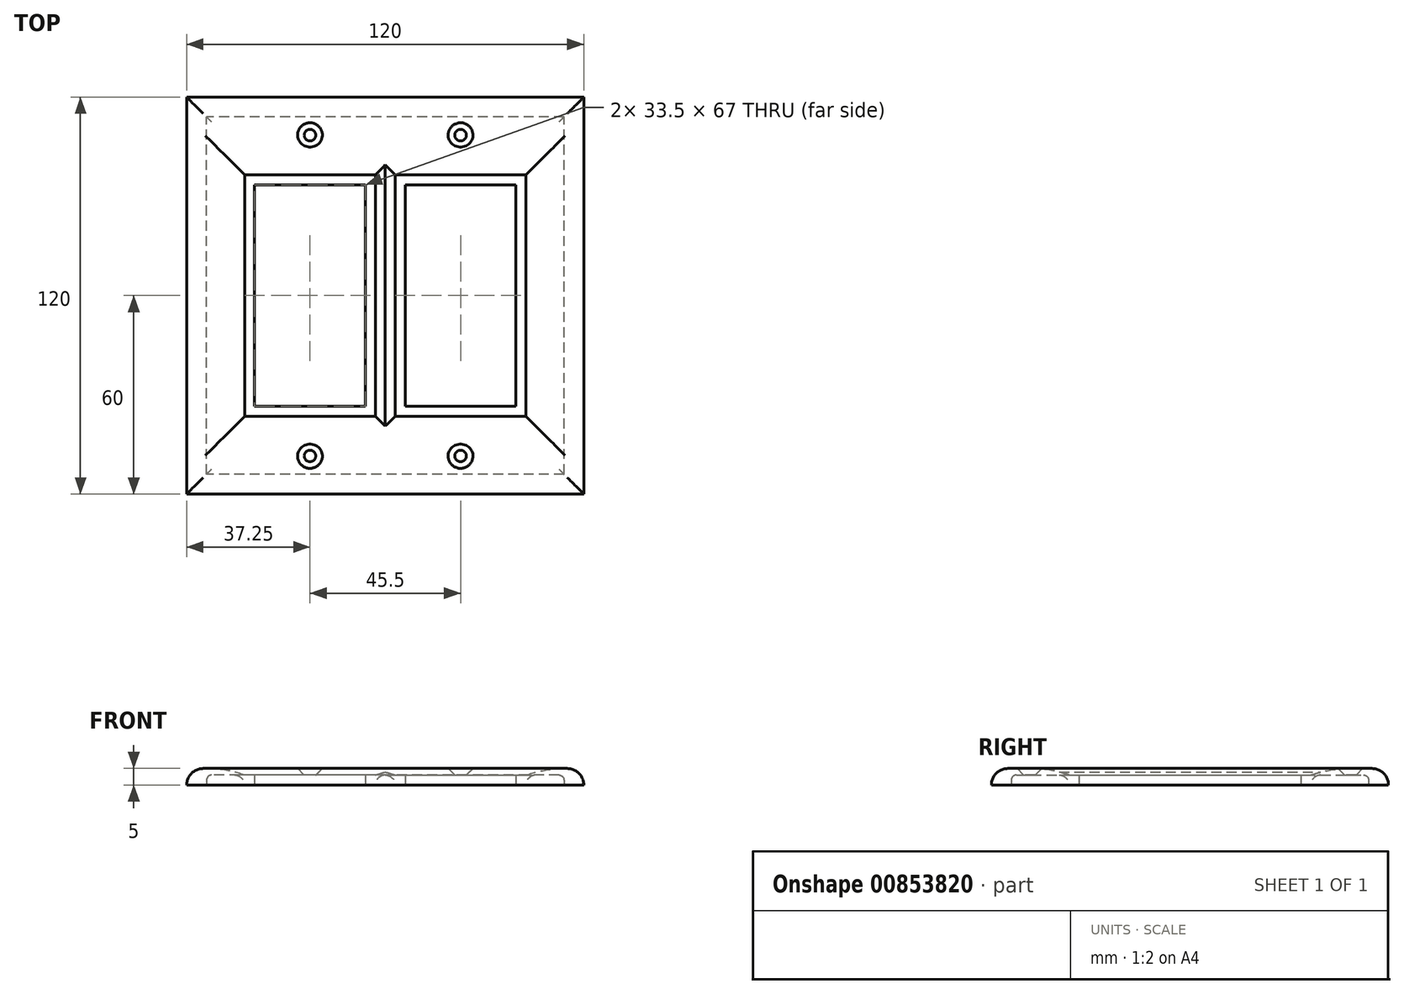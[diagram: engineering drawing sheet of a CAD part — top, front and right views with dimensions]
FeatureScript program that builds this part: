
annotation { "Feature Type Name" : "Feature", "Feature Type Description" : "" }
export const myFeature = defineFeature(function(context is Context, id is Id, definition is map)
    precondition{}
    {
        {
            var Q0;
            Q0=qCreatedBy(makeId("Top.planeOp"),FACE);
            var sketch = newSketch(context, id + "F0", { "sketchPlane" : qUnion([Q0])});
            skLineSegment(sketch, "E0.bottom", {"start": v(60, -60) * mm, "end": v(-60, -60) * mm});
            skLineSegment(sketch, "E0.top", {"start": v(60, 60) * mm, "end": v(-60, 60) * mm});
            skLineSegment(sketch, "E0.left", {"start": v(60, -60) * mm, "end": v(60, 60) * mm});
            skLineSegment(sketch, "E0.right", {"start": v(-60, -60) * mm, "end": v(-60, 60) * mm});
            skPoint(sketch, "E0.middle", {"position": v(0, 0) * mm});
            skLineSegment(sketch, "E1", {"start": v(0, 60) * mm, "end": v(0, -60) * mm, "construction": true});
            skLineSegment(sketch, "E2.bottom", {"start": v(-6, -33.5) * mm, "end": v(-39.5, -33.5) * mm});
            skLineSegment(sketch, "E2.top", {"start": v(-6, 33.5) * mm, "end": v(-39.5, 33.5) * mm});
            skLineSegment(sketch, "E2.left", {"start": v(-6, -33.5) * mm, "end": v(-6, 33.5) * mm});
            skLineSegment(sketch, "E2.right", {"start": v(-39.5, -33.5) * mm, "end": v(-39.5, 33.5) * mm});
            skPoint(sketch, "E2.middle", {"position": v(-22.75, 0) * mm});
            skLineSegment(sketch, "E3", {"start": v(-22.75, 60) * mm, "end": v(-22.75, -60) * mm, "construction": true});
            skPoint(sketch, "E3.startSnap0", {"position": v(-22.75, 33.5) * mm});
            skPoint(sketch, "E3.endSnap0", {"position": v(-22.75, -33.5) * mm});
            skCircle(sketch, "E4", {"center": v(-22.75, 48.5) * mm, "radius": 1.75 * mm});
            skLineSegment(sketch, "E5", {"start": v(-56.43, 0) * mm, "end": v(49.83, 0) * mm, "construction": true});
            skPoint(sketch, "E5.endSnap0", {"position": v(-6, 0) * mm});
            skCircle(sketch, "E6.MirrorC", {"center": v(-22.75, -48.5) * mm, "radius": 1.75 * mm});
            skLineSegment(sketch, "E7.MirrorCS", {"start": v(-6, 60) * mm, "end": v(-6, 33.5) * mm});
            skLineSegment(sketch, "E8.MirrorCS", {"start": v(6, 33.5) * mm, "end": v(39.5, 33.5) * mm});
            skLineSegment(sketch, "E9.MirrorCS", {"start": v(6, -33.5) * mm, "end": v(6, 33.5) * mm});
            skLineSegment(sketch, "E10.MirrorCS", {"start": v(39.5, -33.5) * mm, "end": v(39.5, 33.5) * mm});
            skLineSegment(sketch, "E11.MirrorCS", {"start": v(6, -33.5) * mm, "end": v(39.5, -33.5) * mm});
            skCircle(sketch, "E12.MirrorC", {"center": v(22.75, -48.5) * mm, "radius": 1.75 * mm});
            skCircle(sketch, "E13.MirrorC", {"center": v(22.75, 48.5) * mm, "radius": 1.75 * mm});
            skLineSegment(sketch, "E14.0", {"start": v(54, 54) * mm, "end": v(-54, 54) * mm});
            skLineSegment(sketch, "E14.1", {"start": v(54, -54) * mm, "end": v(54, 54) * mm});
            skLineSegment(sketch, "E14.2", {"start": v(54, -54) * mm, "end": v(-54, -54) * mm});
            skLineSegment(sketch, "E14.3", {"start": v(-54, -54) * mm, "end": v(-54, 54) * mm});
            skPoint(sketch, "E15.MirrorCS.end.orphan", {"position": v(-39.5, 100.5) * mm});
            skPoint(sketch, "E15.MirrorCS.start.orphan", {"position": v(-6, 100.5) * mm});
            skLineSegment(sketch, "E16.0", {"start": v(-42.5, -36.5) * mm, "end": v(-42.5, 36.5) * mm});
            skLineSegment(sketch, "E16.1", {"start": v(-3, -36.5) * mm, "end": v(-42.5, -36.5) * mm});
            skLineSegment(sketch, "E16.2", {"start": v(-3, -36.5) * mm, "end": v(-3, 36.5) * mm});
            skLineSegment(sketch, "E16.3", {"start": v(-3, 36.5) * mm, "end": v(-42.5, 36.5) * mm});
            skLineSegment(sketch, "E17.MirrorCS", {"start": v(3, 36.5) * mm, "end": v(42.5, 36.5) * mm});
            skLineSegment(sketch, "E18.MirrorCS", {"start": v(3, -36.5) * mm, "end": v(3, 36.5) * mm});
            skLineSegment(sketch, "E19.MirrorCS", {"start": v(3, -36.5) * mm, "end": v(42.5, -36.5) * mm});
            skLineSegment(sketch, "E20.MirrorCS", {"start": v(42.5, -36.5) * mm, "end": v(42.5, 36.5) * mm});
            skSolve(sketch);
        }
        {
            var Q0;
            Q0=makeQuery(id+"F0.imprint","IMPRINT",FACE,{"disambiguationData":[TD([[makeQuery(id+"F0.imprint","IMPRINT",EDGE,{"derivedFrom":sQuery(id+"F0.wireOp",EDGE,"E2.bottom")}),1.0]])]});
            var Q1;
            Q1=makeQuery(id+"F0.imprint","IMPRINT",FACE,{"disambiguationData":[TD([[makeQuery(id+"F0.imprint","IMPRINT",EDGE,{"derivedFrom":sQuery(id+"F0.wireOp",EDGE,"E0.bottom")}),-1.0]])]});
            var Q2;
            Q2=makeQuery(id+"F0.imprint","IMPRINT",FACE,{"disambiguationData":[TD([[makeQuery(id+"F0.imprint","IMPRINT",EDGE,{"derivedFrom":sQuery(id+"F0.wireOp",EDGE,"z3IelOHg-C2kR-4Iwb-KN7V-9xO7rj5dRlTz")}),1.0]])]});
            var Q3;
            Q3=makeQuery(id+"F0.imprint","IMPRINT",FACE,{"disambiguationData":[TD([[makeQuery(id+"F0.imprint","IMPRINT",EDGE,{"derivedFrom":sQuery(id+"F0.wireOp",EDGE,"9c88f91e-e929-4360-bad2-47fe56c0c12e0.MirrorC")}),-1.0]])]});
            var Q4;
            Q4=makeQuery(id+"F0.imprint","IMPRINT",FACE,{"disambiguationData":[TD([[makeQuery(id+"F0.imprint","IMPRINT",EDGE,{"derivedFrom":sQuery(id+"F0.wireOp",EDGE,"E8.MirrorCS")}),1.0]])]});
            var Q5;
            Q5=makeQuery(id+"F0.imprint","IMPRINT",FACE,{"disambiguationData":[TD([[makeQuery(id+"F0.imprint","IMPRINT",EDGE,{"derivedFrom":sQuery(id+"F0.wireOp",EDGE,"E4")}),-1.0]])]});
            extrude(context, id + "F1", {"entities" : qUnion([Q0, Q1, Q2, Q3, Q4, Q5]), "depth" : 5 * mm, "offsetDistance" : 25 * mm});
        }
        {
            var Q0;
            Q0=makeQuery(id+"F0.imprint","IMPRINT",FACE,{"disambiguationData":[TD([[makeQuery(id+"F0.imprint","IMPRINT",EDGE,{"derivedFrom":sQuery(id+"F0.wireOp",EDGE,"E4")}),-1.0]])]});
            extrude(context, id + "F2", {"entities" : qUnion([Q0]), "operationType" : NewBodyOperationType.REMOVE, "depth" : 3 * mm, "offsetDistance" : 25 * mm});
        }
        {
            var Q0;
            Q0=makeQuery(id+"F1.opExtrude","CAP_EDGE",EDGE,{"disambiguationData":[OSD([sQuery(id+"F0.wireOp",EDGE,"E0.bottom")])],"isStart":false});
            var Q1;
            Q1=makeQuery(id+"F1.opExtrude","CAP_EDGE",EDGE,{"disambiguationData":[OSD([sQuery(id+"F0.wireOp",EDGE,"E0.left")])],"isStart":false});
            var Q2;
            Q2=makeQuery(id+"F1.opExtrude","CAP_EDGE",EDGE,{"disambiguationData":[OSD([sQuery(id+"F0.wireOp",EDGE,"E0.right")])],"isStart":false});
            var Q3;
            Q3=makeQuery(id+"F1.opExtrude","CAP_EDGE",EDGE,{"disambiguationData":[OSD([sQuery(id+"F0.wireOp",EDGE,"E0.top")])],"isStart":false});
            fillet(context, id + "F3", {"entities" : qUnion([Q0, Q1, Q2, Q3]), "radius" : 5 * mm, "tangentPropagation" : true, "allowEdgeOverflow" : false});
        }
        {
            var Q0;
            Q0=makeQuery(id+"F2.boolean.opBoolean","COPY",EDGE,{"derivedFrom":makeQuery(id+"F2.opExtrude","CAP_EDGE",EDGE,{"disambiguationData":[OSD([sQuery(id+"F0.wireOp",EDGE,"E14.0")])],"isStart":false})});
            var Q1;
            Q1=makeQuery(id+"F2.boolean.opBoolean","COPY",EDGE,{"derivedFrom":makeQuery(id+"F2.opExtrude","CAP_EDGE",EDGE,{"disambiguationData":[OSD([sQuery(id+"F0.wireOp",EDGE,"E14.1")])],"isStart":false})});
            var Q2;
            Q2=makeQuery(id+"F2.boolean.opBoolean","COPY",EDGE,{"derivedFrom":makeQuery(id+"F2.opExtrude","CAP_EDGE",EDGE,{"disambiguationData":[OSD([sQuery(id+"F0.wireOp",EDGE,"E14.2")])],"isStart":false})});
            var Q3;
            Q3=makeQuery(id+"F2.boolean.opBoolean","COPY",EDGE,{"derivedFrom":makeQuery(id+"F2.opExtrude","CAP_EDGE",EDGE,{"disambiguationData":[OSD([sQuery(id+"F0.wireOp",EDGE,"E14.3")])],"isStart":false})});
            fillet(context, id + "F4", {"entities" : qUnion([Q0, Q1, Q2, Q3]), "radius" : 1.5 * mm, "tangentPropagation" : true, "allowEdgeOverflow" : false});
        }
        {
            var Q0;
            Q0=makeQuery(id+"F1.opExtrude","CAP_EDGE",EDGE,{"disambiguationData":[OSD([sQuery(id+"F0.wireOp",EDGE,"E6.MirrorC")])],"isStart":false});
            var Q1;
            Q1=makeQuery(id+"F1.opExtrude","CAP_EDGE",EDGE,{"disambiguationData":[OSD([sQuery(id+"F0.wireOp",EDGE,"E12.MirrorC")])],"isStart":false});
            var Q2;
            Q2=makeQuery(id+"F1.opExtrude","CAP_EDGE",EDGE,{"disambiguationData":[OSD([sQuery(id+"F0.wireOp",EDGE,"E4")])],"isStart":false});
            var Q3;
            Q3=makeQuery(id+"F1.opExtrude","CAP_EDGE",EDGE,{"disambiguationData":[OSD([sQuery(id+"F0.wireOp",EDGE,"E13.MirrorC")])],"isStart":false});
            chamfer(context, id + "F5", {"entities" : qUnion([Q0, Q1, Q2, Q3]), "width" : 2 * mm, "tangentPropagation" : true});
        }
        {
            var Q0;
            Q0=makeQuery(id+"F2.boolean.opBoolean","COPY",EDGE,{"derivedFrom":makeQuery(id+"F2.opExtrude","CAP_EDGE",EDGE,{"disambiguationData":[OSD([sQuery(id+"F0.wireOp",EDGE,"E17.MirrorCS")])],"isStart":false})});
            var Q1;
            Q1=makeQuery(id+"F2.boolean.opBoolean","COPY",EDGE,{"derivedFrom":makeQuery(id+"F2.opExtrude","CAP_EDGE",EDGE,{"disambiguationData":[OSD([sQuery(id+"F0.wireOp",EDGE,"E20.MirrorCS")])],"isStart":false})});
            var Q2;
            Q2=makeQuery(id+"F2.boolean.opBoolean","COPY",EDGE,{"derivedFrom":makeQuery(id+"F2.opExtrude","CAP_EDGE",EDGE,{"disambiguationData":[OSD([sQuery(id+"F0.wireOp",EDGE,"E16.3")])],"isStart":false})});
            var Q3;
            Q3=makeQuery(id+"F2.boolean.opBoolean","COPY",EDGE,{"derivedFrom":makeQuery(id+"F2.opExtrude","CAP_EDGE",EDGE,{"disambiguationData":[OSD([sQuery(id+"F0.wireOp",EDGE,"E16.0")])],"isStart":false})});
            var Q4;
            Q4=makeQuery(id+"F2.boolean.opBoolean","COPY",EDGE,{"derivedFrom":makeQuery(id+"F2.opExtrude","CAP_EDGE",EDGE,{"disambiguationData":[OSD([sQuery(id+"F0.wireOp",EDGE,"E16.1")])],"isStart":false})});
            var Q5;
            Q5=makeQuery(id+"F2.boolean.opBoolean","COPY",EDGE,{"derivedFrom":makeQuery(id+"F2.opExtrude","CAP_EDGE",EDGE,{"disambiguationData":[OSD([sQuery(id+"F0.wireOp",EDGE,"E19.MirrorCS")])],"isStart":false})});
            var Q6;
            Q6=makeQuery(id+"F2.boolean.opBoolean","COPY",EDGE,{"derivedFrom":makeQuery(id+"F2.opExtrude","CAP_EDGE",EDGE,{"disambiguationData":[OSD([sQuery(id+"F0.wireOp",EDGE,"E18.MirrorCS")])],"isStart":false})});
            var Q7;
            Q7=makeQuery(id+"F2.boolean.opBoolean","COPY",EDGE,{"derivedFrom":makeQuery(id+"F2.opExtrude","CAP_EDGE",EDGE,{"disambiguationData":[OSD([sQuery(id+"F0.wireOp",EDGE,"E16.2")])],"isStart":false})});
            fillet(context, id + "F6", {"entities" : qUnion([Q0, Q1, Q2, Q3, Q4, Q5, Q6, Q7]), "radius" : 3 * mm, "tangentPropagation" : true, "allowEdgeOverflow" : false});
        }
        {
            var Q0;
            Q0=makeQuery(id+"F0.imprint","IMPRINT",FACE,{"disambiguationData":[TD([[makeQuery(id+"F0.imprint","IMPRINT",EDGE,{"derivedFrom":sQuery(id+"F0.wireOp",EDGE,"E2.bottom")}),1.0]])]});
            var Q1;
            Q1=makeQuery(id+"F0.imprint","IMPRINT",FACE,{"disambiguationData":[TD([[makeQuery(id+"F0.imprint","IMPRINT",EDGE,{"derivedFrom":sQuery(id+"F0.wireOp",EDGE,"E8.MirrorCS")}),1.0]])]});
            extrude(context, id + "F7", {"entities" : qUnion([Q0, Q1]), "operationType" : NewBodyOperationType.REMOVE, "depth" : 25 * mm, "offsetDistance" : 25 * mm, "hasSecondDirection" : true, "secondDirectionOppositeDirection" : false, "secondDirectionDepth" : 3 * mm});
        }
        {
            var Q0;
            Q0=makeQuery(id+"F7.boolean.opBoolean","INTERSECT",EDGE,{"derivedFrom":[makeQuery(id+"F1.opExtrude","CAP_FACE",FACE,{"disambiguationData":[OSD([sQuery(id+"F0.wireOp",EDGE,"E0.bottom"),sQuery(id+"F0.wireOp",EDGE,"E0.top"),sQuery(id+"F0.wireOp",EDGE,"E0.left"),sQuery(id+"F0.wireOp",EDGE,"E0.right"),sQuery(id+"F0.wireOp",EDGE,"E2.bottom"),sQuery(id+"F0.wireOp",EDGE,"E2.top"),sQuery(id+"F0.wireOp",EDGE,"E2.left"),sQuery(id+"F0.wireOp",EDGE,"E2.right"),sQuery(id+"F0.wireOp",EDGE,"E4"),sQuery(id+"F0.wireOp",EDGE,"E6.MirrorC"),sQuery(id+"F0.wireOp",EDGE,"E8.MirrorCS"),sQuery(id+"F0.wireOp",EDGE,"E9.MirrorCS"),sQuery(id+"F0.wireOp",EDGE,"E10.MirrorCS"),sQuery(id+"F0.wireOp",EDGE,"E11.MirrorCS"),sQuery(id+"F0.wireOp",EDGE,"E12.MirrorC"),sQuery(id+"F0.wireOp",EDGE,"E13.MirrorC")])],"isStart":false}),makeQuery(id+"F7.opExtrude","SWEPT_FACE",FACE,{"disambiguationData":[OSD([sQuery(id+"F0.wireOp",EDGE,"E18.MirrorCS")])]})]});
            var Q1;
            Q1=makeQuery(id+"F7.boolean.opBoolean","INTERSECT",EDGE,{"derivedFrom":[makeQuery(id+"F1.opExtrude","CAP_FACE",FACE,{"disambiguationData":[OSD([sQuery(id+"F0.wireOp",EDGE,"E0.bottom"),sQuery(id+"F0.wireOp",EDGE,"E0.top"),sQuery(id+"F0.wireOp",EDGE,"E0.left"),sQuery(id+"F0.wireOp",EDGE,"E0.right"),sQuery(id+"F0.wireOp",EDGE,"E2.bottom"),sQuery(id+"F0.wireOp",EDGE,"E2.top"),sQuery(id+"F0.wireOp",EDGE,"E2.left"),sQuery(id+"F0.wireOp",EDGE,"E2.right"),sQuery(id+"F0.wireOp",EDGE,"E4"),sQuery(id+"F0.wireOp",EDGE,"E6.MirrorC"),sQuery(id+"F0.wireOp",EDGE,"E8.MirrorCS"),sQuery(id+"F0.wireOp",EDGE,"E9.MirrorCS"),sQuery(id+"F0.wireOp",EDGE,"E10.MirrorCS"),sQuery(id+"F0.wireOp",EDGE,"E11.MirrorCS"),sQuery(id+"F0.wireOp",EDGE,"E12.MirrorC"),sQuery(id+"F0.wireOp",EDGE,"E13.MirrorC")])],"isStart":false}),makeQuery(id+"F7.opExtrude","SWEPT_FACE",FACE,{"disambiguationData":[OSD([sQuery(id+"F0.wireOp",EDGE,"E19.MirrorCS")])]})]});
            var Q2;
            Q2=makeQuery(id+"F7.boolean.opBoolean","INTERSECT",EDGE,{"derivedFrom":[makeQuery(id+"F1.opExtrude","CAP_FACE",FACE,{"disambiguationData":[OSD([sQuery(id+"F0.wireOp",EDGE,"E0.bottom"),sQuery(id+"F0.wireOp",EDGE,"E0.top"),sQuery(id+"F0.wireOp",EDGE,"E0.left"),sQuery(id+"F0.wireOp",EDGE,"E0.right"),sQuery(id+"F0.wireOp",EDGE,"E2.bottom"),sQuery(id+"F0.wireOp",EDGE,"E2.top"),sQuery(id+"F0.wireOp",EDGE,"E2.left"),sQuery(id+"F0.wireOp",EDGE,"E2.right"),sQuery(id+"F0.wireOp",EDGE,"E4"),sQuery(id+"F0.wireOp",EDGE,"E6.MirrorC"),sQuery(id+"F0.wireOp",EDGE,"E8.MirrorCS"),sQuery(id+"F0.wireOp",EDGE,"E9.MirrorCS"),sQuery(id+"F0.wireOp",EDGE,"E10.MirrorCS"),sQuery(id+"F0.wireOp",EDGE,"E11.MirrorCS"),sQuery(id+"F0.wireOp",EDGE,"E12.MirrorC"),sQuery(id+"F0.wireOp",EDGE,"E13.MirrorC")])],"isStart":false}),makeQuery(id+"F7.opExtrude","SWEPT_FACE",FACE,{"disambiguationData":[OSD([sQuery(id+"F0.wireOp",EDGE,"E16.1")])]})]});
            var Q3;
            Q3=makeQuery(id+"F7.boolean.opBoolean","INTERSECT",EDGE,{"derivedFrom":[makeQuery(id+"F1.opExtrude","CAP_FACE",FACE,{"disambiguationData":[OSD([sQuery(id+"F0.wireOp",EDGE,"E0.bottom"),sQuery(id+"F0.wireOp",EDGE,"E0.top"),sQuery(id+"F0.wireOp",EDGE,"E0.left"),sQuery(id+"F0.wireOp",EDGE,"E0.right"),sQuery(id+"F0.wireOp",EDGE,"E2.bottom"),sQuery(id+"F0.wireOp",EDGE,"E2.top"),sQuery(id+"F0.wireOp",EDGE,"E2.left"),sQuery(id+"F0.wireOp",EDGE,"E2.right"),sQuery(id+"F0.wireOp",EDGE,"E4"),sQuery(id+"F0.wireOp",EDGE,"E6.MirrorC"),sQuery(id+"F0.wireOp",EDGE,"E8.MirrorCS"),sQuery(id+"F0.wireOp",EDGE,"E9.MirrorCS"),sQuery(id+"F0.wireOp",EDGE,"E10.MirrorCS"),sQuery(id+"F0.wireOp",EDGE,"E11.MirrorCS"),sQuery(id+"F0.wireOp",EDGE,"E12.MirrorC"),sQuery(id+"F0.wireOp",EDGE,"E13.MirrorC")])],"isStart":false}),makeQuery(id+"F7.opExtrude","SWEPT_FACE",FACE,{"disambiguationData":[OSD([sQuery(id+"F0.wireOp",EDGE,"E16.0")])]})]});
            var Q4;
            Q4=makeQuery(id+"F7.boolean.opBoolean","INTERSECT",EDGE,{"derivedFrom":[makeQuery(id+"F1.opExtrude","CAP_FACE",FACE,{"disambiguationData":[OSD([sQuery(id+"F0.wireOp",EDGE,"E0.bottom"),sQuery(id+"F0.wireOp",EDGE,"E0.top"),sQuery(id+"F0.wireOp",EDGE,"E0.left"),sQuery(id+"F0.wireOp",EDGE,"E0.right"),sQuery(id+"F0.wireOp",EDGE,"E2.bottom"),sQuery(id+"F0.wireOp",EDGE,"E2.top"),sQuery(id+"F0.wireOp",EDGE,"E2.left"),sQuery(id+"F0.wireOp",EDGE,"E2.right"),sQuery(id+"F0.wireOp",EDGE,"E4"),sQuery(id+"F0.wireOp",EDGE,"E6.MirrorC"),sQuery(id+"F0.wireOp",EDGE,"E8.MirrorCS"),sQuery(id+"F0.wireOp",EDGE,"E9.MirrorCS"),sQuery(id+"F0.wireOp",EDGE,"E10.MirrorCS"),sQuery(id+"F0.wireOp",EDGE,"E11.MirrorCS"),sQuery(id+"F0.wireOp",EDGE,"E12.MirrorC"),sQuery(id+"F0.wireOp",EDGE,"E13.MirrorC")])],"isStart":false}),makeQuery(id+"F7.opExtrude","SWEPT_FACE",FACE,{"disambiguationData":[OSD([sQuery(id+"F0.wireOp",EDGE,"E16.3")])]})]});
            var Q5;
            Q5=makeQuery(id+"F7.boolean.opBoolean","INTERSECT",EDGE,{"derivedFrom":[makeQuery(id+"F1.opExtrude","CAP_FACE",FACE,{"disambiguationData":[OSD([sQuery(id+"F0.wireOp",EDGE,"E0.bottom"),sQuery(id+"F0.wireOp",EDGE,"E0.top"),sQuery(id+"F0.wireOp",EDGE,"E0.left"),sQuery(id+"F0.wireOp",EDGE,"E0.right"),sQuery(id+"F0.wireOp",EDGE,"E2.bottom"),sQuery(id+"F0.wireOp",EDGE,"E2.top"),sQuery(id+"F0.wireOp",EDGE,"E2.left"),sQuery(id+"F0.wireOp",EDGE,"E2.right"),sQuery(id+"F0.wireOp",EDGE,"E4"),sQuery(id+"F0.wireOp",EDGE,"E6.MirrorC"),sQuery(id+"F0.wireOp",EDGE,"E8.MirrorCS"),sQuery(id+"F0.wireOp",EDGE,"E9.MirrorCS"),sQuery(id+"F0.wireOp",EDGE,"E10.MirrorCS"),sQuery(id+"F0.wireOp",EDGE,"E11.MirrorCS"),sQuery(id+"F0.wireOp",EDGE,"E12.MirrorC"),sQuery(id+"F0.wireOp",EDGE,"E13.MirrorC")])],"isStart":false}),makeQuery(id+"F7.opExtrude","SWEPT_FACE",FACE,{"disambiguationData":[OSD([sQuery(id+"F0.wireOp",EDGE,"E17.MirrorCS")])]})]});
            var Q6;
            Q6=makeQuery(id+"F7.boolean.opBoolean","INTERSECT",EDGE,{"derivedFrom":[makeQuery(id+"F1.opExtrude","CAP_FACE",FACE,{"disambiguationData":[OSD([sQuery(id+"F0.wireOp",EDGE,"E0.bottom"),sQuery(id+"F0.wireOp",EDGE,"E0.top"),sQuery(id+"F0.wireOp",EDGE,"E0.left"),sQuery(id+"F0.wireOp",EDGE,"E0.right"),sQuery(id+"F0.wireOp",EDGE,"E2.bottom"),sQuery(id+"F0.wireOp",EDGE,"E2.top"),sQuery(id+"F0.wireOp",EDGE,"E2.left"),sQuery(id+"F0.wireOp",EDGE,"E2.right"),sQuery(id+"F0.wireOp",EDGE,"E4"),sQuery(id+"F0.wireOp",EDGE,"E6.MirrorC"),sQuery(id+"F0.wireOp",EDGE,"E8.MirrorCS"),sQuery(id+"F0.wireOp",EDGE,"E9.MirrorCS"),sQuery(id+"F0.wireOp",EDGE,"E10.MirrorCS"),sQuery(id+"F0.wireOp",EDGE,"E11.MirrorCS"),sQuery(id+"F0.wireOp",EDGE,"E12.MirrorC"),sQuery(id+"F0.wireOp",EDGE,"E13.MirrorC")])],"isStart":false}),makeQuery(id+"F7.opExtrude","SWEPT_FACE",FACE,{"disambiguationData":[OSD([sQuery(id+"F0.wireOp",EDGE,"E20.MirrorCS")])]})]});
            var Q7;
            Q7=makeQuery(id+"F7.boolean.opBoolean","INTERSECT",EDGE,{"derivedFrom":[makeQuery(id+"F1.opExtrude","CAP_FACE",FACE,{"disambiguationData":[OSD([sQuery(id+"F0.wireOp",EDGE,"E0.bottom"),sQuery(id+"F0.wireOp",EDGE,"E0.top"),sQuery(id+"F0.wireOp",EDGE,"E0.left"),sQuery(id+"F0.wireOp",EDGE,"E0.right"),sQuery(id+"F0.wireOp",EDGE,"E2.bottom"),sQuery(id+"F0.wireOp",EDGE,"E2.top"),sQuery(id+"F0.wireOp",EDGE,"E2.left"),sQuery(id+"F0.wireOp",EDGE,"E2.right"),sQuery(id+"F0.wireOp",EDGE,"E4"),sQuery(id+"F0.wireOp",EDGE,"E6.MirrorC"),sQuery(id+"F0.wireOp",EDGE,"E8.MirrorCS"),sQuery(id+"F0.wireOp",EDGE,"E9.MirrorCS"),sQuery(id+"F0.wireOp",EDGE,"E10.MirrorCS"),sQuery(id+"F0.wireOp",EDGE,"E11.MirrorCS"),sQuery(id+"F0.wireOp",EDGE,"E12.MirrorC"),sQuery(id+"F0.wireOp",EDGE,"E13.MirrorC")])],"isStart":false}),makeQuery(id+"F7.opExtrude","SWEPT_FACE",FACE,{"disambiguationData":[OSD([sQuery(id+"F0.wireOp",EDGE,"E16.2")])]})]});
            fillet(context, id + "F8", {"entities" : qUnion([Q0, Q1, Q2, Q3, Q4, Q5, Q6, Q7]), "radius" : 36.2 * mm, "tangentPropagation" : true, "allowEdgeOverflow" : false});
        }
    });
